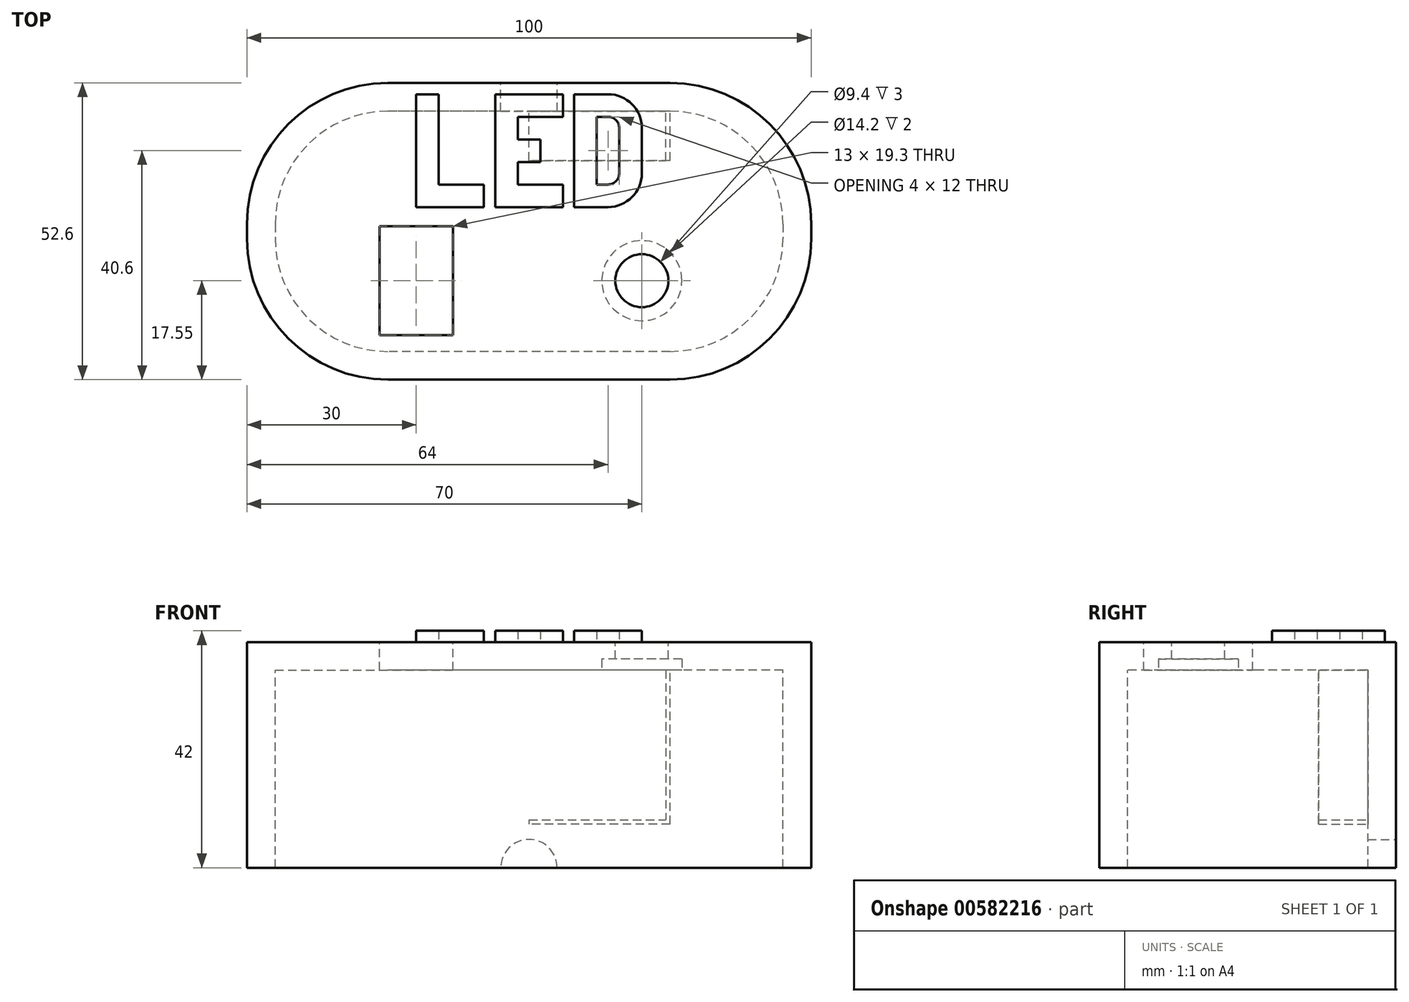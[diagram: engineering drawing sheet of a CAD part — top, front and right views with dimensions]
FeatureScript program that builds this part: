
annotation { "Feature Type Name" : "Feature", "Feature Type Description" : "" }
export const myFeature = defineFeature(function(context is Context, id is Id, definition is map)
    precondition{}
    {
        {
            var Q0;
            Q0=qCreatedBy(makeId("Top.planeOp"),FACE);
            cPlane(context, id + "F0", {"entities" : qUnion([Q0]), "cplaneType" : CPlaneType.OFFSET, "offset" : 35 * mm, "width" : 150 * mm, "height" : 150 * mm});
        }
        {
            var Q0;
            Q0=qCreatedBy(id+"F0.planeOp",FACE);
            var sketch = newSketch(context, id + "F1", { "sketchPlane" : qUnion([Q0])});
            skLineSegment(sketch, "E0.bottom", {"start": v(25, 26.3) * mm, "end": v(-25, 26.3) * mm});
            skLineSegment(sketch, "E0.top", {"start": v(25, -26.3) * mm, "end": v(-25, -26.3) * mm});
            skLineSegment(sketch, "E0.left", {"start": v(50, 1.3) * mm, "end": v(50, -1.3) * mm});
            skLineSegment(sketch, "E0.right", {"start": v(-50, 1.3) * mm, "end": v(-50, -1.3) * mm});
            skPoint(sketch, "E0.middle", {"position": v(0, 0) * mm});
            skPoint(sketch, "E1.visualSharp", {"position": v(-50, 26.3) * mm});
            skArc(sketch, "E1.filletArc", {"start": v(-25, 26.3) * mm, "mid": v(-42.68, 18.98) * mm, "end": v(-50, 1.3) * mm});
            skPoint(sketch, "E2.visualSharp", {"position": v(-50, -26.3) * mm});
            skArc(sketch, "E2.filletArc", {"start": v(-50, -1.3) * mm, "mid": v(-42.68, -18.98) * mm, "end": v(-25, -26.3) * mm});
            skPoint(sketch, "E3.visualSharp", {"position": v(50, -26.3) * mm});
            skArc(sketch, "E3.filletArc", {"start": v(25, -26.3) * mm, "mid": v(42.68, -18.98) * mm, "end": v(50, -1.3) * mm});
            skPoint(sketch, "E4.visualSharp", {"position": v(50, 26.3) * mm});
            skArc(sketch, "E4.filletArc", {"start": v(50, 1.3) * mm, "mid": v(42.68, 18.98) * mm, "end": v(25, 26.3) * mm});
            skSolve(sketch);
        }
        {
            var Q0;
            Q0=makeQuery(id+"F1.imprint","IMPRINT",FACE,{"disambiguationData":[TD([[makeQuery(id+"F1.imprint","IMPRINT",EDGE,{"derivedFrom":sQuery(id+"F1.wireOp",EDGE,"E0.bottom")}),1.0]])]});
            extrude(context, id + "F2", {"entities" : qUnion([Q0]), "depth" : 5 * mm, "offsetDistance" : 25 * mm});
        }
        {
            var Q0;
            Q0=makeQuery(id+"F2.opExtrude","CAP_FACE",FACE,{"disambiguationData":[OSD([sQuery(id+"F1.wireOp",EDGE,"E0.bottom"),sQuery(id+"F1.wireOp",EDGE,"E0.top"),sQuery(id+"F1.wireOp",EDGE,"E1.filletArc"),sQuery(id+"F1.wireOp",EDGE,"E2.filletArc"),sQuery(id+"F1.wireOp",EDGE,"E3.filletArc"),sQuery(id+"F1.wireOp",EDGE,"E4.filletArc")])],"isStart":false});
            var sketch = newSketch(context, id + "F3", { "sketchPlane" : qUnion([Q0])});
            skLineSegment(sketch, "E5.bottom", {"start": v(-13.5, 0.9) * mm, "end": v(-26.5, 0.9) * mm});
            skLineSegment(sketch, "E5.top", {"start": v(-13.5, -18.4) * mm, "end": v(-26.5, -18.4) * mm});
            skLineSegment(sketch, "E5.left", {"start": v(-13.5, 0.9) * mm, "end": v(-13.5, -18.4) * mm});
            skLineSegment(sketch, "E5.right", {"start": v(-26.5, 0.9) * mm, "end": v(-26.5, -18.4) * mm});
            skPoint(sketch, "E5.middle", {"position": v(-20, -8.75) * mm});
            skCircle(sketch, "E6", {"center": v(20, -8.75) * mm, "radius": 4.7 * mm});
            skLineSegment(sketch, "E7.bottom", {"start": v(-25, 24.3) * mm, "end": v(25, 24.3) * mm});
            skLineSegment(sketch, "E7.top", {"start": v(-25, 4.3) * mm, "end": v(14, 4.3) * mm});
            skLineSegment(sketch, "E7.left", {"start": v(-25, 24.3) * mm, "end": v(-25, 4.3) * mm});
            skLineSegment(sketch, "E7.right", {"start": v(25, 24.3) * mm, "end": v(25, 4.3) * mm});
            skLineSegment(sketch, "E8", {"start": v(-20, 24.3) * mm, "end": v(-16, 24.3) * mm});
            skLineSegment(sketch, "E9", {"start": v(-16, 24.3) * mm, "end": v(-16, 8.3) * mm});
            skLineSegment(sketch, "E10", {"start": v(-16, 8.3) * mm, "end": v(-8, 8.3) * mm});
            skLineSegment(sketch, "E11", {"start": v(-8, 8.3) * mm, "end": v(-8, 4.3) * mm});
            skLineSegment(sketch, "E12", {"start": v(-8, 4.3) * mm, "end": v(-20, 4.3) * mm});
            skLineSegment(sketch, "E13", {"start": v(-20, 4.3) * mm, "end": v(-20, 24.3) * mm});
            skLineSegment(sketch, "E14", {"start": v(-6, 24.3) * mm, "end": v(-6, 4.3) * mm});
            skLineSegment(sketch, "E15", {"start": v(-6, 24.3) * mm, "end": v(6, 24.3) * mm});
            skLineSegment(sketch, "E16", {"start": v(6, 24.3) * mm, "end": v(6, 20.3) * mm});
            skLineSegment(sketch, "E17", {"start": v(6, 20.3) * mm, "end": v(-2, 20.3) * mm});
            skLineSegment(sketch, "E18", {"start": v(-2, 20.3) * mm, "end": v(-2, 16.3) * mm});
            skLineSegment(sketch, "E19", {"start": v(-2, 16.3) * mm, "end": v(2, 16.3) * mm});
            skLineSegment(sketch, "E20", {"start": v(2, 16.3) * mm, "end": v(2, 12.3) * mm});
            skLineSegment(sketch, "E21", {"start": v(2, 12.3) * mm, "end": v(-2, 12.3) * mm});
            skLineSegment(sketch, "E22", {"start": v(-2, 12.3) * mm, "end": v(-2, 8.3) * mm});
            skLineSegment(sketch, "E23", {"start": v(-2, 8.3) * mm, "end": v(6, 8.3) * mm});
            skLineSegment(sketch, "E24", {"start": v(6, 8.3) * mm, "end": v(6, 4.3) * mm});
            skLineSegment(sketch, "E25", {"start": v(6, 4.3) * mm, "end": v(-6, 4.3) * mm});
            skLineSegment(sketch, "E26", {"start": v(8, 24.3) * mm, "end": v(8, 4.3) * mm});
            skLineSegment(sketch, "E27", {"start": v(8, 24.3) * mm, "end": v(20, 24.3) * mm});
            skLineSegment(sketch, "E28", {"start": v(20, 18.3) * mm, "end": v(20, 10.3) * mm});
            skLineSegment(sketch, "E29", {"start": v(20, 4.3) * mm, "end": v(8, 4.3) * mm});
            skLineSegment(sketch, "E30", {"start": v(12, 20.3) * mm, "end": v(14, 20.3) * mm});
            skLineSegment(sketch, "E31", {"start": v(16, 18.3) * mm, "end": v(16, 10.3) * mm});
            skLineSegment(sketch, "E32", {"start": v(14, 8.3) * mm, "end": v(12, 8.3) * mm});
            skLineSegment(sketch, "E33", {"start": v(12, 8.3) * mm, "end": v(12, 20.3) * mm});
            skLineSegment(sketch, "E34", {"start": v(8, 24.3) * mm, "end": v(12, 24.3) * mm});
            skLineSegment(sketch, "E35", {"start": v(8, 4.3) * mm, "end": v(12, 4.3) * mm});
            skPoint(sketch, "E36.visualSharp", {"position": v(16, 20.3) * mm});
            skArc(sketch, "E36.filletArc", {"start": v(16, 18.3) * mm, "mid": v(15.41, 19.71) * mm, "end": v(14, 20.3) * mm});
            skPoint(sketch, "E37.visualSharp", {"position": v(16, 8.3) * mm});
            skArc(sketch, "E37.filletArc", {"start": v(14, 8.3) * mm, "mid": v(15.41, 8.89) * mm, "end": v(16, 10.3) * mm});
            skLineSegment(sketch, "E38", {"start": v(-25, 24.3) * mm, "end": v(14, 24.3) * mm});
            skLineSegment(sketch, "E39", {"start": v(-25, 4.3) * mm, "end": v(25, 4.3) * mm});
            skArc(sketch, "E40.filletArc", {"start": v(20, 18.3) * mm, "mid": v(18.24, 22.54) * mm, "end": v(14, 24.3) * mm});
            skPoint(sketch, "E41.newPointB", {"position": v(25, 4.3) * mm});
            skArc(sketch, "E41.filletArc", {"start": v(14, 4.3) * mm, "mid": v(18.24, 6.06) * mm, "end": v(20, 10.3) * mm});
            skSolve(sketch);
        }
        {
            var Q0;
            Q0=makeQuery(id+"F3.imprint","IMPRINT",FACE,{"disambiguationData":[TD([[makeQuery(id+"F3.imprint","IMPRINT",EDGE,{"derivedFrom":sQuery(id+"F3.wireOp",EDGE,"E5.bottom")}),1.0]])]});
            var Q1;
            Q1=makeQuery(id+"F3.imprint","IMPRINT",FACE,{"disambiguationData":[TD([[makeQuery(id+"F3.imprint","IMPRINT",EDGE,{"derivedFrom":sQuery(id+"F3.wireOp",EDGE,"E6")}),1.0]])]});
            extrude(context, id + "F4", {"entities" : qUnion([Q0, Q1]), "operationType" : NewBodyOperationType.REMOVE, "endBound" : BoundingType.UP_TO_NEXT, "oppositeDirection" : true, "depth" : 25 * mm, "offsetDistance" : 25 * mm});
        }
        {
            var Q0;
            Q0=makeQuery(id+"F1.imprint","IMPRINT",FACE,{"disambiguationData":[TD([[makeQuery(id+"F1.imprint","IMPRINT",EDGE,{"derivedFrom":sQuery(id+"F1.wireOp",EDGE,"E0.bottom")}),1.0]])]});
            var sketch = newSketch(context, id + "F5", { "sketchPlane" : qUnion([Q0])});
            skCircle(sketch, "E42", {"center": v(20, -8.75) * mm, "radius": 7.1 * mm});
            skCircle(sketch, "E43", {"center": v(20, -8.75) * mm, "radius": 12.55 * mm, "construction": true});
            skLineSegment(sketch, "E44", {"start": v(20, -8.75) * mm, "end": v(27.1, -8.75) * mm, "construction": true});
            skLineSegment(sketch, "E45", {"start": v(27.1, -8.75) * mm, "end": v(32.55, -8.75) * mm, "construction": true});
            skLineSegment(sketch, "E46.bottom", {"start": v(28.65, -9.8) * mm, "end": v(31, -9.8) * mm});
            skLineSegment(sketch, "E46.top", {"start": v(28.65, -7.7) * mm, "end": v(31, -7.7) * mm});
            skLineSegment(sketch, "E46.left", {"start": v(27.6, -8.75) * mm, "end": v(27.6, -8.75) * mm});
            skLineSegment(sketch, "E46.right", {"start": v(32.05, -8.75) * mm, "end": v(32.05, -8.75) * mm});
            skPoint(sketch, "E46.middle", {"position": v(29.83, -8.75) * mm});
            skPoint(sketch, "E47.visualSharp", {"position": v(27.6, -9.8) * mm});
            skArc(sketch, "E47.filletArc", {"start": v(27.6, -8.75) * mm, "mid": v(27.9, -9.5) * mm, "end": v(28.65, -9.8) * mm});
            skPoint(sketch, "E48.visualSharp", {"position": v(27.6, -7.7) * mm});
            skArc(sketch, "E48.filletArc", {"start": v(28.65, -7.7) * mm, "mid": v(27.9, -8) * mm, "end": v(27.6, -8.75) * mm});
            skPoint(sketch, "E49.visualSharp", {"position": v(32.05, -7.7) * mm});
            skArc(sketch, "E49.filletArc", {"start": v(32.05, -8.75) * mm, "mid": v(31.74, -8) * mm, "end": v(31, -7.7) * mm});
            skPoint(sketch, "E50.visualSharp", {"position": v(32.05, -9.8) * mm});
            skArc(sketch, "E50.filletArc", {"start": v(31, -9.8) * mm, "mid": v(31.74, -9.5) * mm, "end": v(32.05, -8.75) * mm});
            skLineSegment(sketch, "E51", {"start": v(20, 3.8) * mm, "end": v(20, -8.75) * mm, "construction": true});
            skLineSegment(sketch, "E52", {"start": v(20, -8.75) * mm, "end": v(28.87, -17.62) * mm, "construction": true});
            skLineSegment(sketch, "E53", {"start": v(20, -8.75) * mm, "end": v(11.13, 0.12) * mm, "construction": true});
            skLineSegment(sketch, "E54", {"start": v(20, -8.75) * mm, "end": v(11.13, -17.62) * mm, "construction": true});
            skLineSegment(sketch, "E55", {"start": v(20, -8.75) * mm, "end": v(28.87, 0.12) * mm, "construction": true});
            skLineSegment(sketch, "E56", {"start": v(20, -8.75) * mm, "end": v(20, -21.3) * mm, "construction": true});
            skLineSegment(sketch, "E57.1.0", {"start": v(26.86, -3.38) * mm, "end": v(28.52, -1.71) * mm});
            skArc(sketch, "E57.1.1", {"start": v(25.37, -3.38) * mm, "mid": v(26.12, -3.68) * mm, "end": v(26.86, -3.38) * mm});
            skArc(sketch, "E57.1.2", {"start": v(25.37, -1.9) * mm, "mid": v(25.07, -2.63) * mm, "end": v(25.37, -3.38) * mm});
            skLineSegment(sketch, "E57.1.3", {"start": v(25.37, -1.9) * mm, "end": v(27.04, -0.23) * mm});
            skArc(sketch, "E57.1.4", {"start": v(28.52, -0.23) * mm, "mid": v(27.78, 0.08) * mm, "end": v(27.04, -0.23) * mm});
            skArc(sketch, "E57.1.5", {"start": v(28.52, -1.71) * mm, "mid": v(28.83, -0.97) * mm, "end": v(28.52, -0.23) * mm});
            skLineSegment(sketch, "E57.2.0", {"start": v(21.05, -0.1) * mm, "end": v(21.05, 2.25) * mm});
            skArc(sketch, "E57.2.1", {"start": v(20, -1.15) * mm, "mid": v(20.74, -0.84) * mm, "end": v(21.05, -0.1) * mm});
            skArc(sketch, "E57.2.2", {"start": v(18.95, -0.1) * mm, "mid": v(19.26, -0.84) * mm, "end": v(20, -1.15) * mm});
            skLineSegment(sketch, "E57.2.3", {"start": v(18.95, -0.1) * mm, "end": v(18.95, 2.25) * mm});
            skArc(sketch, "E57.2.4", {"start": v(20, 3.3) * mm, "mid": v(19.26, 3) * mm, "end": v(18.95, 2.25) * mm});
            skArc(sketch, "E57.2.5", {"start": v(21.05, 2.25) * mm, "mid": v(20.74, 3) * mm, "end": v(20, 3.3) * mm});
            skLineSegment(sketch, "E57.3.0", {"start": v(14.63, -1.9) * mm, "end": v(12.96, -0.23) * mm});
            skArc(sketch, "E57.3.1", {"start": v(14.63, -3.38) * mm, "mid": v(14.93, -2.63) * mm, "end": v(14.63, -1.9) * mm});
            skArc(sketch, "E57.3.2", {"start": v(13.14, -3.38) * mm, "mid": v(13.88, -3.68) * mm, "end": v(14.63, -3.38) * mm});
            skLineSegment(sketch, "E57.3.3", {"start": v(13.14, -3.38) * mm, "end": v(11.48, -1.71) * mm});
            skArc(sketch, "E57.3.4", {"start": v(11.48, -0.23) * mm, "mid": v(11.17, -0.97) * mm, "end": v(11.48, -1.71) * mm});
            skArc(sketch, "E57.3.5", {"start": v(12.96, -0.23) * mm, "mid": v(12.22, 0.08) * mm, "end": v(11.48, -0.23) * mm});
            skLineSegment(sketch, "E57.4.0", {"start": v(11.35, -7.7) * mm, "end": v(9, -7.7) * mm});
            skArc(sketch, "E57.4.1", {"start": v(12.4, -8.75) * mm, "mid": v(12.1, -8) * mm, "end": v(11.35, -7.7) * mm});
            skArc(sketch, "E57.4.2", {"start": v(11.35, -9.8) * mm, "mid": v(12.1, -9.5) * mm, "end": v(12.4, -8.75) * mm});
            skLineSegment(sketch, "E57.4.3", {"start": v(11.35, -9.8) * mm, "end": v(9, -9.8) * mm});
            skArc(sketch, "E57.4.4", {"start": v(7.95, -8.75) * mm, "mid": v(8.26, -9.5) * mm, "end": v(9, -9.8) * mm});
            skArc(sketch, "E57.4.5", {"start": v(9, -7.7) * mm, "mid": v(8.26, -8) * mm, "end": v(7.95, -8.75) * mm});
            skLineSegment(sketch, "E57.5.0", {"start": v(13.14, -14.12) * mm, "end": v(11.48, -15.79) * mm});
            skArc(sketch, "E57.5.1", {"start": v(14.63, -14.12) * mm, "mid": v(13.88, -13.82) * mm, "end": v(13.14, -14.12) * mm});
            skArc(sketch, "E57.5.2", {"start": v(14.63, -15.6) * mm, "mid": v(14.93, -14.87) * mm, "end": v(14.63, -14.12) * mm});
            skLineSegment(sketch, "E57.5.3", {"start": v(14.63, -15.6) * mm, "end": v(12.96, -17.27) * mm});
            skArc(sketch, "E57.5.4", {"start": v(11.48, -17.27) * mm, "mid": v(12.22, -17.58) * mm, "end": v(12.96, -17.27) * mm});
            skArc(sketch, "E57.5.5", {"start": v(11.48, -15.79) * mm, "mid": v(11.17, -16.53) * mm, "end": v(11.48, -17.27) * mm});
            skLineSegment(sketch, "E57.6.0", {"start": v(18.95, -17.4) * mm, "end": v(18.95, -19.75) * mm});
            skArc(sketch, "E57.6.1", {"start": v(20, -16.35) * mm, "mid": v(19.26, -16.66) * mm, "end": v(18.95, -17.4) * mm});
            skArc(sketch, "E57.6.2", {"start": v(21.05, -17.4) * mm, "mid": v(20.74, -16.66) * mm, "end": v(20, -16.35) * mm});
            skLineSegment(sketch, "E57.6.3", {"start": v(21.05, -17.4) * mm, "end": v(21.05, -19.75) * mm});
            skArc(sketch, "E57.6.4", {"start": v(20, -20.8) * mm, "mid": v(20.74, -20.5) * mm, "end": v(21.05, -19.75) * mm});
            skArc(sketch, "E57.6.5", {"start": v(18.95, -19.75) * mm, "mid": v(19.26, -20.5) * mm, "end": v(20, -20.8) * mm});
            skLineSegment(sketch, "E57.7.0", {"start": v(25.37, -15.6) * mm, "end": v(27.04, -17.27) * mm});
            skArc(sketch, "E57.7.1", {"start": v(25.37, -14.12) * mm, "mid": v(25.07, -14.87) * mm, "end": v(25.37, -15.6) * mm});
            skArc(sketch, "E57.7.2", {"start": v(26.86, -14.12) * mm, "mid": v(26.12, -13.82) * mm, "end": v(25.37, -14.12) * mm});
            skLineSegment(sketch, "E57.7.3", {"start": v(26.86, -14.12) * mm, "end": v(28.52, -15.79) * mm});
            skArc(sketch, "E57.7.4", {"start": v(28.52, -17.27) * mm, "mid": v(28.83, -16.53) * mm, "end": v(28.52, -15.79) * mm});
            skArc(sketch, "E57.7.5", {"start": v(27.04, -17.27) * mm, "mid": v(27.78, -17.58) * mm, "end": v(28.52, -17.27) * mm});
            skLineSegment(sketch, "E58", {"start": v(0, 0) * mm, "end": v(0, -25) * mm, "construction": true});
            skLineSegment(sketch, "E59", {"start": v(20, -8.75) * mm, "end": v(7.45, -8.75) * mm, "construction": true});
            skSolve(sketch);
        }
        {
            var Q0;
            Q0=makeQuery(id+"F5.imprint","IMPRINT",FACE,{"disambiguationData":[TD([[makeQuery(id+"F5.imprint","IMPRINT",EDGE,{"derivedFrom":sQuery(id+"F5.wireOp",EDGE,"E42")}),1.0]])]});
            extrude(context, id + "F6", {"entities" : qUnion([Q0]), "operationType" : NewBodyOperationType.REMOVE, "depth" : 2 * mm, "offsetDistance" : 25 * mm});
        }
        {
            var Q0;
            Q0=makeQuery(id+"F1.imprint","IMPRINT",FACE,{"disambiguationData":[TD([[makeQuery(id+"F1.imprint","IMPRINT",EDGE,{"derivedFrom":sQuery(id+"F1.wireOp",EDGE,"E0.bottom")}),1.0]])]});
            var sketch = newSketch(context, id + "F7", { "sketchPlane" : qUnion([Q0])});
            skLineSegment(sketch, "E60.bottom", {"start": v(25, 26.3) * mm, "end": v(-25, 26.3) * mm});
            skLineSegment(sketch, "E60.top", {"start": v(25, -26.3) * mm, "end": v(-25, -26.3) * mm});
            skLineSegment(sketch, "E60.left", {"start": v(50, 1.3) * mm, "end": v(50, -1.3) * mm});
            skLineSegment(sketch, "E60.right", {"start": v(-50, 1.3) * mm, "end": v(-50, -1.3) * mm});
            skPoint(sketch, "E60.middle", {"position": v(0, 0) * mm});
            skPoint(sketch, "E61.visualSharp", {"position": v(-50, 26.3) * mm});
            skArc(sketch, "E61.filletArc", {"start": v(-25, 26.3) * mm, "mid": v(-42.68, 18.98) * mm, "end": v(-50, 1.3) * mm});
            skPoint(sketch, "E62.visualSharp", {"position": v(-50, -26.3) * mm});
            skArc(sketch, "E62.filletArc", {"start": v(-50, -1.3) * mm, "mid": v(-42.68, -18.98) * mm, "end": v(-25, -26.3) * mm});
            skPoint(sketch, "E63.visualSharp", {"position": v(50, -26.3) * mm});
            skArc(sketch, "E63.filletArc", {"start": v(25, -26.3) * mm, "mid": v(42.68, -18.98) * mm, "end": v(50, -1.3) * mm});
            skPoint(sketch, "E64.visualSharp", {"position": v(50, 26.3) * mm});
            skArc(sketch, "E64.filletArc", {"start": v(50, 1.3) * mm, "mid": v(42.68, 18.98) * mm, "end": v(25, 26.3) * mm});
            skLineSegment(sketch, "E65.bottom", {"start": v(25, 21.3) * mm, "end": v(-25, 21.3) * mm});
            skLineSegment(sketch, "E65.top", {"start": v(25, -21.3) * mm, "end": v(-25, -21.3) * mm});
            skLineSegment(sketch, "E65.left", {"start": v(45, 1.3) * mm, "end": v(45, -1.3) * mm});
            skLineSegment(sketch, "E65.right", {"start": v(-45, 1.3) * mm, "end": v(-45, -1.3) * mm});
            skPoint(sketch, "E66.visualSharp", {"position": v(-45, 21.3) * mm});
            skArc(sketch, "E66.filletArc", {"start": v(-25, 21.3) * mm, "mid": v(-39.14, 15.44) * mm, "end": v(-45, 1.3) * mm});
            skPoint(sketch, "E67.visualSharp", {"position": v(-45, -21.3) * mm});
            skArc(sketch, "E67.filletArc", {"start": v(-45, -1.3) * mm, "mid": v(-39.14, -15.44) * mm, "end": v(-25, -21.3) * mm});
            skPoint(sketch, "E68.visualSharp", {"position": v(45, -21.3) * mm});
            skArc(sketch, "E68.filletArc", {"start": v(25, -21.3) * mm, "mid": v(39.14, -15.44) * mm, "end": v(45, -1.3) * mm});
            skPoint(sketch, "E69.visualSharp", {"position": v(45, 21.3) * mm});
            skArc(sketch, "E69.filletArc", {"start": v(45, 1.3) * mm, "mid": v(39.14, 15.44) * mm, "end": v(25, 21.3) * mm});
            skSolve(sketch);
        }
        {
            var Q0;
            Q0=makeQuery(id+"F7.imprint","IMPRINT",FACE,{"disambiguationData":[TD([[makeQuery(id+"F7.imprint","IMPRINT",EDGE,{"derivedFrom":sQuery(id+"F7.wireOp",EDGE,"E60.bottom")}),1.0]])]});
            extrude(context, id + "F8", {"entities" : qUnion([Q0]), "oppositeDirection" : true, "depth" : 35 * mm, "offsetDistance" : 25 * mm});
        }
        {
            var Q0;
            Q0=makeQuery(id+"F8.boolean.opBoolean","MERGE",FACE,{"derivedFrom":[makeQuery(id+"F2.opExtrude","SWEPT_FACE",FACE,{"disambiguationData":[OSD([sQuery(id+"F1.wireOp",EDGE,"E0.bottom")])]}),makeQuery(id+"F8.opExtrude","SWEPT_FACE",FACE,{"disambiguationData":[OSD([sQuery(id+"F7.wireOp",EDGE,"E60.bottom")])]})]});
            var sketch = newSketch(context, id + "F9", { "sketchPlane" : qUnion([Q0])});
            skLineSegment(sketch, "E70.bottom", {"start": v(-5, 0) * mm, "end": v(5, 0) * mm});
            skLineSegment(sketch, "E70.top", {"start": v(0, 5) * mm, "end": v(0, 5) * mm});
            skLineSegment(sketch, "E70.left", {"start": v(-5, 0) * mm, "end": v(-5, 0) * mm});
            skLineSegment(sketch, "E70.right", {"start": v(5, 0) * mm, "end": v(5, 0) * mm});
            skPoint(sketch, "E70.middle", {"position": v(0, 2.5) * mm});
            skPoint(sketch, "E71.visualSharp", {"position": v(-5, 5) * mm});
            skArc(sketch, "E71.filletArc", {"start": v(0, 5) * mm, "mid": v(-3.54, 3.54) * mm, "end": v(-5, 0) * mm});
            skPoint(sketch, "E72.visualSharp", {"position": v(5, 5) * mm});
            skArc(sketch, "E72.filletArc", {"start": v(5, 0) * mm, "mid": v(3.54, 3.54) * mm, "end": v(0, 5) * mm});
            skSolve(sketch);
        }
        {
            var Q0;
            Q0=makeQuery(id+"F9.imprint","IMPRINT",FACE,{"disambiguationData":[TD([[makeQuery(id+"F9.imprint","IMPRINT",EDGE,{"derivedFrom":sQuery(id+"F9.wireOp",EDGE,"E70.bottom")}),1.0]])]});
            extrude(context, id + "F10", {"entities" : qUnion([Q0]), "operationType" : NewBodyOperationType.REMOVE, "endBound" : BoundingType.UP_TO_NEXT, "oppositeDirection" : true, "depth" : 25 * mm, "offsetDistance" : 25 * mm});
        }
        {
            var Q0;
            Q0=makeQuery(id+"F8.opExtrude","SWEPT_FACE",FACE,{"disambiguationData":[OSD([sQuery(id+"F7.wireOp",EDGE,"E65.bottom")])]});
            var sketch = newSketch(context, id + "F11", { "sketchPlane" : qUnion([Q0])});
            skLineSegment(sketch, "E73.bottom", {"start": v(-24.25, 35) * mm, "end": v(24.25, 35) * mm});
            skLineSegment(sketch, "E73.top", {"start": v(-24.25, 8.5) * mm, "end": v(24.25, 8.5) * mm});
            skLineSegment(sketch, "E73.left", {"start": v(-24.25, 35) * mm, "end": v(-24.25, 8.5) * mm});
            skLineSegment(sketch, "E73.right", {"start": v(24.25, 35) * mm, "end": v(24.25, 8.5) * mm});
            skLineSegment(sketch, "E74", {"start": v(0, 5) * mm, "end": v(0, 35) * mm, "construction": true});
            skLineSegment(sketch, "E75", {"start": v(-24.25, 21.75) * mm, "end": v(0, 21.75) * mm, "construction": true});
            skLineSegment(sketch, "E76", {"start": v(0, 21.75) * mm, "end": v(24.25, 21.75) * mm, "construction": true});
            skLineSegment(sketch, "E77", {"start": v(0, 35) * mm, "end": v(0, 5) * mm, "construction": true});
            skLineSegment(sketch, "E78", {"start": v(25, 35) * mm, "end": v(25, 7.75) * mm});
            skLineSegment(sketch, "E79", {"start": v(25, 7.75) * mm, "end": v(-24.25, 7.75) * mm});
            skLineSegment(sketch, "E80", {"start": v(-24.25, 7.75) * mm, "end": v(-24.25, 8.5) * mm});
            skLineSegment(sketch, "E81", {"start": v(0, 8.5) * mm, "end": v(0, 7.75) * mm});
            skSolve(sketch);
        }
        {
            var Q0;
            {var subQ5=sQuery(id+"F11.wireOp",EDGE,"E73.right");Q0=makeQuery(id+"F11.imprint","IMPRINT",FACE,{"disambiguationData":[TD([[makeQuery(id+"F11.imprint","IMPRINT",EDGE,{"derivedFrom":subQ5}),1.0]])]});}
            extrude(context, id + "F12", {"entities" : qUnion([Q0]), "operationType" : NewBodyOperationType.ADD, "depth" : 8.75 * mm, "offsetDistance" : 25 * mm});
        }
        {
            var Q0;
            Q0=makeQuery(id+"F3.imprint","IMPRINT",FACE,{"disambiguationData":[TD([[makeQuery(id+"F3.imprint","IMPRINT",EDGE,{"derivedFrom":sQuery(id+"F3.wireOp",EDGE,"E5.bottom")}),-1.0]])]});
            var sketch = newSketch(context, id + "F13", { "sketchPlane" : qUnion([Q0])});
            skSolve(sketch);
        }
        {
            var Q0;
            {var subQ3=sQuery(id+"F3.wireOp",EDGE,"E9");Q0=makeQuery(id+"F3.imprint","IMPRINT",FACE,{"disambiguationData":[TD([[makeQuery(id+"F3.imprint","IMPRINT",EDGE,{"derivedFrom":subQ3}),-1.0]])]});}
            var Q1;
            {var subQ2=sQuery(id+"F3.wireOp",EDGE,"E14");Q1=makeQuery(id+"F3.imprint","IMPRINT",FACE,{"disambiguationData":[TD([[makeQuery(id+"F3.imprint","IMPRINT",EDGE,{"derivedFrom":subQ2}),1.0]])]});}
            var Q2;
            {var subQ0=sQuery(id+"F3.wireOp",EDGE,"E26");Q2=makeQuery(id+"F3.imprint","IMPRINT",FACE,{"disambiguationData":[TD([[makeQuery(id+"F3.imprint","IMPRINT",EDGE,{"derivedFrom":subQ0}),1.0]])]});}
            extrude(context, id + "F14", {"entities" : qUnion([Q0, Q1, Q2]), "depth" : 2 * mm, "offsetDistance" : 25 * mm});
        }
    });
